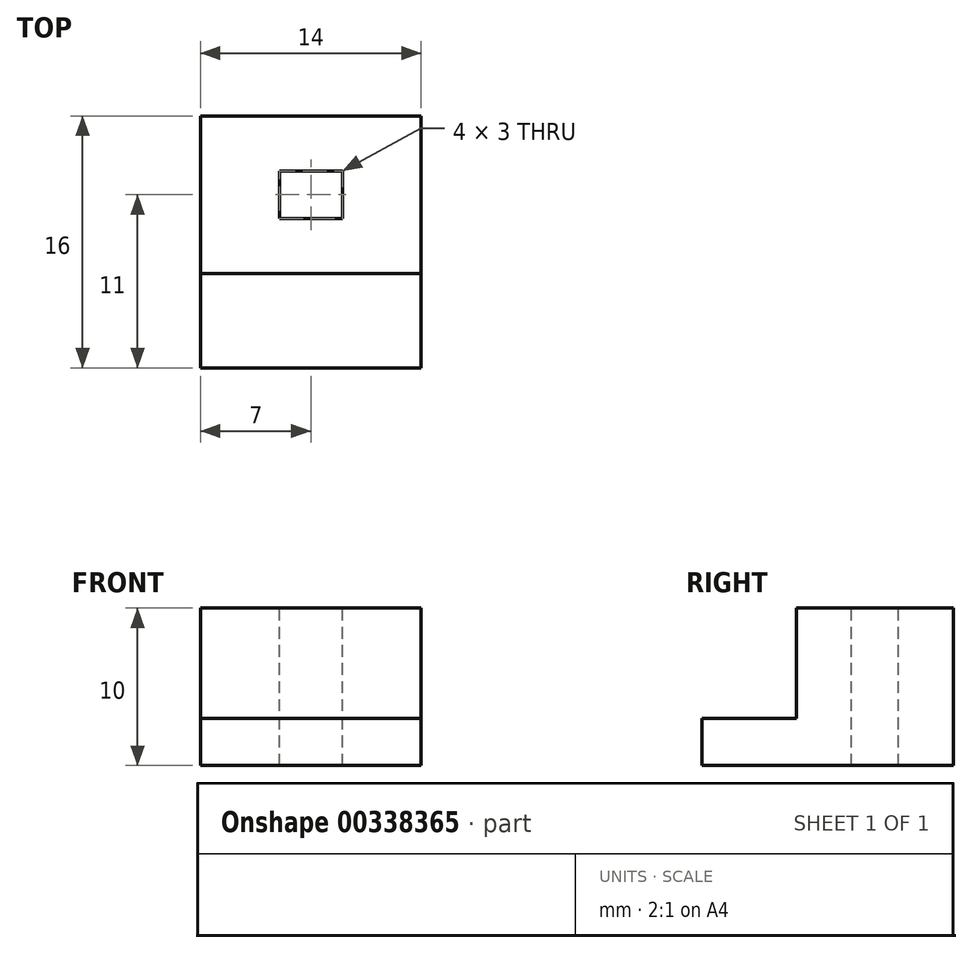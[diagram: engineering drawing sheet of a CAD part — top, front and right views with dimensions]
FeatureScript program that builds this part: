
annotation { "Feature Type Name" : "Feature", "Feature Type Description" : "" }
export const myFeature = defineFeature(function(context is Context, id is Id, definition is map)
    precondition{}
    {
        {
            var Q0;
            Q0=qCreatedBy(makeId("Top.planeOp"),FACE);
            var sketch = newSketch(context, id + "F0", { "sketchPlane" : qUnion([Q0])});
            skLineSegment(sketch, "E0.bottom", {"start": v(0, 0) * mm, "end": v(14, 0) * mm});
            skLineSegment(sketch, "E0.top", {"start": v(0, -16) * mm, "end": v(14, -16) * mm});
            skLineSegment(sketch, "E0.left", {"start": v(0, 0) * mm, "end": v(0, -16) * mm});
            skLineSegment(sketch, "E0.right", {"start": v(14, 0) * mm, "end": v(14, -16) * mm});
            skSolve(sketch);
        }
        {
            var Q0;
            Q0 = qSketchRegion(id + "F0", true);
            extrude(context, id + "F1", {"entities" : qUnion([Q0]), "depth" : 10 * mm});
        }
        {
            var Q0;
            Q0=makeQuery(id+"F1.opExtrude","CAP_FACE",FACE,{"disambiguationData":[OSD([sQuery(id+"F0.wireOp",EDGE,"E0.bottom"),sQuery(id+"F0.wireOp",EDGE,"E0.top"),sQuery(id+"F0.wireOp",EDGE,"E0.left"),sQuery(id+"F0.wireOp",EDGE,"E0.right")])],"isStart":false});
            var sketch = newSketch(context, id + "F2", { "sketchPlane" : qUnion([Q0])});
            skLineSegment(sketch, "E1.bottom", {"start": v(0, -16) * mm, "end": v(14, -16) * mm});
            skLineSegment(sketch, "E1.top", {"start": v(0, -10) * mm, "end": v(14, -10) * mm});
            skLineSegment(sketch, "E1.left", {"start": v(0, -16) * mm, "end": v(0, -10) * mm});
            skLineSegment(sketch, "E1.right", {"start": v(14, -16) * mm, "end": v(14, -10) * mm});
            skSolve(sketch);
        }
        {
            var Q0;
            Q0 = qSketchRegion(id + "F2", true);
            extrude(context, id + "F3", {"entities" : qUnion([Q0]), "operationType" : NewBodyOperationType.REMOVE, "oppositeDirection" : true, "depth" : 7 * mm});
        }
        {
            var Q0;
            Q0=makeQuery(id+"F1.opExtrude","CAP_FACE",FACE,{"disambiguationData":[OSD([sQuery(id+"F0.wireOp",EDGE,"E0.bottom"),sQuery(id+"F0.wireOp",EDGE,"E0.top"),sQuery(id+"F0.wireOp",EDGE,"E0.left"),sQuery(id+"F0.wireOp",EDGE,"E0.right")])],"isStart":false});
            var sketch = newSketch(context, id + "F4", { "sketchPlane" : qUnion([Q0])});
            skLineSegment(sketch, "E2.bottom", {"start": v(5, -3.5) * mm, "end": v(9, -3.5) * mm});
            skLineSegment(sketch, "E2.top", {"start": v(5, -6.5) * mm, "end": v(9, -6.5) * mm});
            skLineSegment(sketch, "E2.left", {"start": v(5, -3.5) * mm, "end": v(5, -6.5) * mm});
            skLineSegment(sketch, "E2.right", {"start": v(9, -3.5) * mm, "end": v(9, -6.5) * mm});
            skPoint(sketch, "E2.middle", {"position": v(7, -5) * mm});
            skPoint(sketch, "E2.middle.positionSnap0", {"position": v(0, -5) * mm});
            skPoint(sketch, "E2.middle.positionSnap1", {"position": v(7, 0) * mm});
            skPoint(sketch, "E2.centerSnap0", {"position": v(0, -5) * mm});
            skPoint(sketch, "E2.centerSnap1", {"position": v(7, 0) * mm});
            skSolve(sketch);
        }
        {
            var Q0;
            Q0 = qSketchRegion(id + "F4", true);
            extrude(context, id + "F5", {"entities" : qUnion([Q0]), "operationType" : NewBodyOperationType.REMOVE, "endBound" : BoundingType.THROUGH_ALL, "oppositeDirection" : true, "depth" : 25 * mm});
        }
    });
